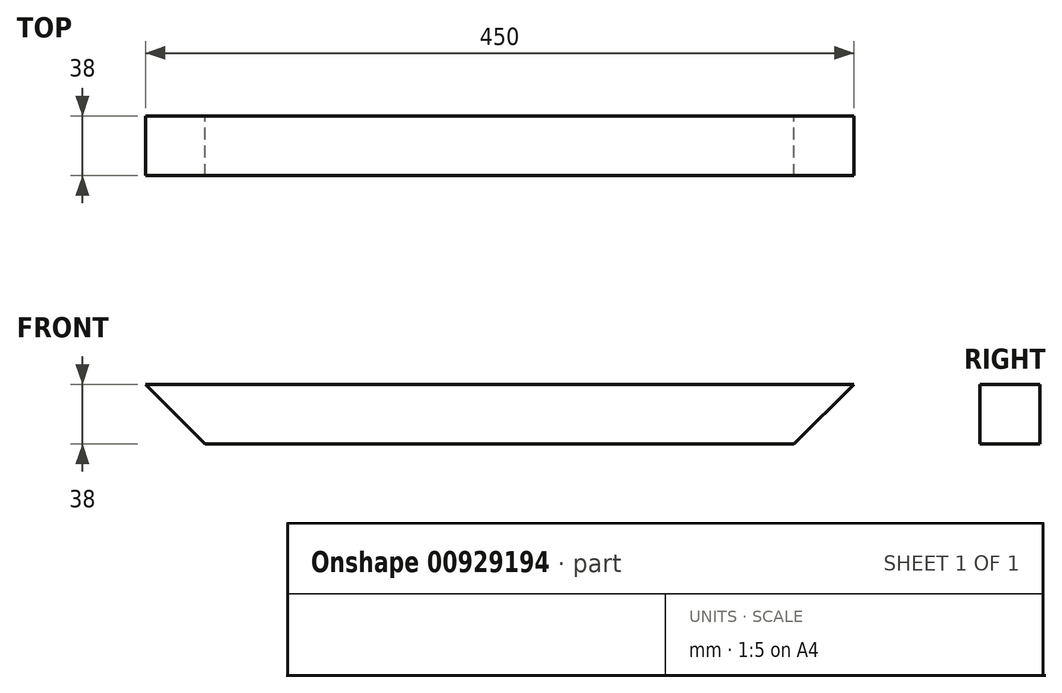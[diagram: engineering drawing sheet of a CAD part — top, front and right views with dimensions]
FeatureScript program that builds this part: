
annotation { "Feature Type Name" : "Feature", "Feature Type Description" : "" }
export const myFeature = defineFeature(function(context is Context, id is Id, definition is map)
    precondition{}
    {
        {
            var Q0;
            Q0=qCreatedBy(makeId("Front.planeOp"),FACE);
            var sketch = newSketch(context, id + "F0", { "sketchPlane" : qUnion([Q0])});
            skLineSegment(sketch, "E0", {"start": v(-169.53, 0) * mm, "end": v(280.47, 0) * mm});
            skLineSegment(sketch, "E1", {"start": v(280.47, 0) * mm, "end": v(242.47, -38) * mm});
            skLineSegment(sketch, "E2", {"start": v(242.47, -38) * mm, "end": v(-131.53, -38) * mm});
            skLineSegment(sketch, "E3", {"start": v(-131.53, -38) * mm, "end": v(-169.53, 0) * mm});
            skSolve(sketch);
        }
        {
            var Q0;
            Q0=qSketchRegion(id+"F0",true);
            extrude(context, id + "F1", {"entities" : qUnion([Q0]), "depth" : 38 * mm, "offsetDistance" : 25 * mm});
        }
    });
